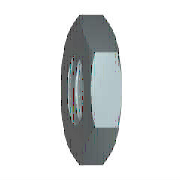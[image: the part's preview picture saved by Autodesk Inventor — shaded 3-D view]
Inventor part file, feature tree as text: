
AUTODESK INVENTOR PART (.ipt)
format: ipt  version: 2015 (Build 190159000, 159)  size: 164,864 bytes
history: native  units: mm (DEFAULTED — no unit token found)
features: sketch x3, other x2, extrude x1, hole x1, plane x1
ambient origin geometry x7: Origin, YZ Plane, XZ Plane, X Axis, Y Axis, Z Axis, Center Point
bodies: Body1 (feature_tree)
feature tree (8):
  extrude  "Bryła"  Depth=11.547005mm
  other  "Faza1"
  hole  "Gwint"  [1 undecoded]
  other  "Work Axis1"
  plane  "Work Plane1"
  sketch  "Szkic1"
  sketch  "Szkic2"
  sketch  "Szkic3"
note: 1 required parameter value undecoded (feature->parameter linkage not recoverable at this tier; creation-order binding heuristic only, values carry confidence <= 0.55)
